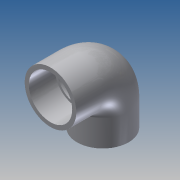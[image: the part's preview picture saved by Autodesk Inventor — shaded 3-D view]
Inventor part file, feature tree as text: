
AUTODESK INVENTOR PART (.ipt)
format: ipt  version: 2014 SP1 (Build 180222100, 222)  size: 259,072 bytes
history: native  units: in
note: dims shown in document units (in); Inventor stores cm internally (conversion verified against a paired STEP export)
features: sketch x4, extrude x2, plane x1, sweep x1, other x1
ambient origin geometry x8: Origin, YZ Plane, XZ Plane, XY Plane, X Axis, Y Axis, Z Axis, Center Point
bodies: Solid1 (feature_tree)
feature tree (9):
  extrude  "Extrusion1"  Depth=0.2362in
  plane  "Work Plane1"
  extrude  "Extrusion2"  [1 undecoded]
  sweep  "Sweep1"
  sketch  "Sketch1"  dims[d0=2.4803in d1=0.2362in]
  sketch  "Sketch3"  dims[d2=1.4961in d3=0.0in d4=-1.4961in]
  sketch  "Sketch5"  dims[d5=2.9528in d6=1.4961in]
  other  "2D Equation Curve1"
  sketch  "Sketch6"  dims[d7=0.2362in d8=1.4961in d9=0.0in d11=0.0in d12=35.4331in d13=2.2047in d14=0.0in]
note: 1 required parameter value undecoded (feature->parameter linkage not recoverable at this tier; creation-order binding heuristic only, values carry confidence <= 0.55)
